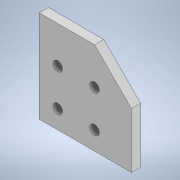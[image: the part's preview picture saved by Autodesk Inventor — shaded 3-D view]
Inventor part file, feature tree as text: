
AUTODESK INVENTOR PART (.ipt)
format: ipt  version: 2020 (Build 240168000, 168)  size: 109,568 bytes
history: native  units: in
note: dims shown in document units (in); Inventor stores cm internally (conversion verified against a paired STEP export)
features: extrude x1, sketch x1
ambient origin geometry x8: Origin, YZ Plane, XZ Plane, XY Plane, X Axis, Y Axis, Z Axis, Center Point
bodies: Solid1 (feature_tree)
feature tree (2):
  extrude  "Extrusion1"  Depth=0.25in
  sketch  "Sketch1"  dims[d10=2.5in d11=2.0in d12=1.5in d14=1.5in d15=1.0in d16=1.0in d17=0.256in d18=0.5in d19=0.5in d20=0.7874in d22=1.0in d23=0.7874in d25=1.0in d28=0.25in d29=0.0in]
